# Revit family: HUNTER_PROS-04 Fixed Arc and Adjustable Pro Nozzles
name_source: partatom
category: Sprinklers
revit_build: Autodesk Revit 2017 (Build: 20160225_1515(x64)
units: mm (PartAtom-declared; Revit-internal decimal feet)

## family parameters
Always vertical = Yes
Cut with Voids When Loaded = No
Maintain Annotation Orientation = No
OmniClass Number = 23.11.27.15.11.11
OmniClass Title = Installed Sprinkler Heads
Part Type = Normal
Room Calculation Point = No
Round Connector Dimension = Use Diameter
Shared = Yes
Work Plane-Based = No

## types (24) — shared parameters
Assembly Code = G2050700
Body Height = 155 mm  [stored 0.50853 ft]
Body Material = Hunter® ABS Plastic
Connection_Dia = 15 mm  [stored 0.0492126 ft]
Diameter = 610 mm
Exposed Diameter = 57 mm
Keynote = 328423.02
Manufacturer = Hunter® Industries
Nozzle URL = https://www.hunterindustries.com
Pop Up Height = 100 mm  [stored 0.328084 ft]
Pop Up Material = Hunter® ABS Plastic
Pressure = 210.0 kPa
Seal = Hunter® White Flex Seal
Show 2D Symbol = Yes
Show Water Spray = Yes
Type Comments = Pro-Spray® PROS-04
Type Image = <None>
URL = https://www.hunterindustries.com
Water = Water
Water Spray Pattern = Water Arc

## per-type parameters (varying)
| type | Arc Max | Arc Min | Description | Inlet Size | Model | Nozzle Size | Nozzle_Ref | Trajectory Angle | Trajectory Radius |
| PROS-04-5 Blue-F_360-1.5m | 360.00° | 360.00° | ProSpray® PROS-04 10cm PopUp with Pro-Spray Fixed Arc (5 Blue) Nozzle/ F_360° Arc Position | 1/2'' NPT | PROS-04-5F | Hunter®Pro-Spray Fixed Arc (5 Blue) Nozzle/ F_360° Arc Position | 5000 | 1.00° | 1500 mm  [stored 4.92126 ft] |
| PROS-04-8 Brown-F_360_2.4m | 360.00° | 360.00° | ProSpray® PROS-04 10cm PopUp with Pro-Spray Fixed Arc (8 Brown) Nozzle / F_360° Arc Position | 1/2'' NPT | PROS-04-8F | Hunter®Pro-Spray Fixed Arc (8 Brown) Nozzle / F_360° Arc Position | 8000 | 2.00° | 2400 mm  [stored 7.87402 ft] |
| PROS-04-10 Red-F_360-3.0m | 360.00° | 360.00° | ProSpray® PROS-04 10cm PopUp with Pro-Spray Fixed Arc (10 Red) Nozzle/ F_360° Arc Position | 1/2'' NPT | PROS-04-10F | Hunter®Pro-Spray Fixed Arc (10 Red) Nozzle/ F_360° Arc Position | 10000 | 15.00° | 3000 mm  [stored 9.84252 ft] |
| PROS-04-12 Green-F_360-3.7m | 360.00° | 360.00° | ProSpray® PROS-04 10cm PopUp with Pro-Spray Fixed Arc (12 Green) Nozzle / F_360° Arc Position | 1/2'' NPT | PROS-04-12F | Hunter®Pro-Spray Fixed Arc (12 Green) Nozzle / F_360° Arc Position | 12000 | 28.00° | 3700 mm |
| PROS-04-15 Black-F_360-4.6m | 360.00° | 360.00° | ProSpray® PROS-04 10cm PopUp with Pro-Spray Fixed Arc (15 Black) Nozzle / F_360° Arc Position | 1/2'' NPT | PROS-04-15F | Hunter®Pro-Spray Fixed Arc (15 Black) Nozzle / F_360° Arc Position | 15000 | 28.00° | 4600 mm |
| PROS-04-4A_Lt. Green_1.2m | 360.00° | 0.00° | ProSpray® PROS-04 10cm PopUp with Pro Adjustable 4A-Lt. Green Nozzle | 1/2" NPT | PROS-04-4A | Hunter® Pro Adjustable (4A) Lt.Green Nozzle | 4 | 5.00° | 1200 mm  [stored 3.93701 ft] |
| PROS-04-6A_Lt. Blue_1.8m | 360.00° | 0.00° | ProSpray® PROS-04 10cm PopUp with Pro Adjustable  6A-Lt. Blue Nozzle | 1/2" NPT | PROS-04-6A | Hunter® Pro Adjustable (6A) Lt.Blue Nozzle | 6 | 5.00° | 1800 mm |
| PROS-04-8A_Brown_2.4m | 360.00° | 0.00° | ProSpray® PROS-04 10cm PopUp with Pro Adjustable  8A-Brown Nozzle | 1/2" NPT | PROS-04-8A Brown | Hunter® Pro Adjustable (8A) Brown Nozzle | 8 | 5.00° | 2400 mm  [stored 7.87402 ft] |
| PROS-04-10A_Red_3.0m | 360.00° | 0.00° | ProSpray® PROS-04 10cm PopUp with Pro Adjustable  10A-Red Nozzle | 1/2" NPT | PROS-04-10A Red | Hunter® Pro Adjustable (10A) Red Nozzle | 10 | 15.00° | 3000 mm  [stored 9.84252 ft] |
| PROS-04-12A_Green_3.7m | 360.00° | 0.00° | ProSpray® PROS-04 10cm PopUp with Pro Adjustable  12A-Green Nozzle | 1/2" NPT | PROS-04-12A Green | Hunter® Pro Adjustable (12A) Green Nozzle | 12 | 28.00° | 3700 mm |
| PROS-04-17A_Grey_5.2m | 360.00° | 0.00° | ProSpray® PROS-04 10cm PopUp with Pro Adjustable  17A-Grey Nozzle | 1/2" NPT | PROS-04-17A Grey | Hunter® Pro Adjustable (17A) Grey Nozzle | 17 | 28.00° | 5200 mm |
| PROS-04-15A_Black_4.6m | 360.00° | 0.00° | ProSpray® PROS-04 10cm PopUp with Pro Adjustable  15A-Black Nozzle | 1/2" NPT | PROS-04-15A Black | Hunter® Pro Adjustable (15A) Black Nozzle | 15 | 28.00° | 4600 mm |
| PROS-04-8 Brown-Q_90-2.4m | 90.00° | 90.00° | ProSpray® PROS-04 10cm PopUp with Pro-Spray Fixed Arc (8 Brown) Nozzle / Q_90° Arc Position | 1/2'' NPT | PROS-04-8Q | Hunter®Pro-Spray Fixed Arc (8 Brown) Nozzle / Q_90° Arc Position | 80 | 2.00° | 2400 mm  [stored 7.87402 ft] |
| PROS-04-8 Brown-H_180-2.4m | 180.00° | 180.00° | ProSpray® PROS-04 10cm PopUp with PPro-Spray Fixed Arc (8 Brown) Nozzle / H_180° Arc Position | 1/2'' NPT | PROS-04-8H | Hunter®Pro-Spray Fixed Arc (8 Brown) Nozzle / H_180° Arc Position | 800 | 2.00° | 2400 mm  [stored 7.87402 ft] |
| PROS-04-5 Blue-H_180-1.5m | 180.00° | 180.00° | ProSpray® PROS-04 10cm PopUp with Pro-Spray Fixed Arc (5 Blue) Nozzle/ H_180° Arc Position | 1/2'' NPT | PROS-04-5H | Hunter®Pro-Spray Fixed Arc (5 Blue) Nozzle/ H_180° Arc Position | 500 | 1.00° | 1500 mm  [stored 4.92126 ft] |
| PROS-04-5 Blue-Q_90-1.5m | 90.00° | 90.00° | ProSpray® PROS-04 10cm PopUp with Pro-Spray Fixed Arc (5 Blue) Nozzle / Q_90° Arc Position | 1/2'' NPT | PROS-04-5Q | Hunter®Pro-Spray Fixed Arc (5 Blue) Nozzle / Q_90° Arc Position | 50 | 1.00° | 1500 mm  [stored 4.92126 ft] |
| PROS-04-17 Grey-H_180-5.2m | 180.00° | 180.00° | ProSpray® PROS-04 10cm PopUp with Pro-Spray Fixed Arc (17 Grey) Nozzle / H_180° Arc Position | 1/2'' NPT | PROS-04-17H | Hunter®Pro-Spray Fixed Arc (17 Grey) Nozzle / H_180° Arc Position | 1700 | 28.00° | 5200 mm |
| PROS-04-17 Grey-Q_90-5.2m | 90.00° | 90.00° | ProSpray® PROS-04 10cm PopUp with Pro-Spray Fixed Arc (17 Grey) Nozzle / Q_90° Arc Position | 1/2'' NPT | PROS-04-17Q | Hunter®Pro-Spray Fixed Arc (17 Grey) Nozzle / Q_90° Arc Position | 170 | 28.00° | 5200 mm |
| PROS-04-15 Black-H_180-4.6m | 180.00° | 180.00° | ProSpray® PROS-04 10cm PopUp with Pro-Spray Fixed Arc (15 Black) Nozzle / H_180° Arc Position | 1/2'' NPT | PROS-04-15H | Hunter®Pro-Spray Fixed Arc (15 Black) Nozzle / H_180° Arc Position | 1500 | 28.00° | 4600 mm |
| PROS-04-15 Black-Q_90-4.6m | 90.00° | 90.00° | ProSpray® PROS-04 10cm PopUp with Pro-Spray Fixed Arc (15 Black) Nozzle / Q_90° Arc Position | 1/2'' NPT | PROS-04-15Q | Hunter®Pro-Spray Fixed Arc (15 Black) Nozzle / Q_90° Arc Position | 150 | 28.00° | 4600 mm |
| PROS-04-12 Green-H_180-3.7m | 180.00° | 180.00° | ProSpray® PROS-04 10cm PopUp with Pro-Spray Fixed Arc (12 Green) Nozzle / H_180° Arc Position | 1/2'' NPT | PROS-04-12H | Hunter®Pro-Spray Fixed Arc (12 Green) Nozzle / H_180° Arc Position | 1200 | 28.00° | 3700 mm |
| PROS-04-12 Green-Q_90-3.7m | 90.00° | 90.00° | ProSpray® PROS-04 10cm PopUp with Pro-Spray Fixed Arc (12 Green) Nozzle / Q_90° Arc Position | 1/2'' NPT | PROS-04-12Q | Hunter®Pro-Spray Fixed Arc (12 Green) Nozzle / Q_90° Arc Position | 120 | 28.00° | 3700 mm |
| PROS-04-10 Red-Q_90-3.0m | 90.00° | 90.00° | ProSpray® PROS-04 10cm PopUp with Pro-Spray Fixed Arc (10 Red) Nozzle / Q_90° Arc Position | 1/2'' NPT | PROS-04-10Q | Hunter®Pro-Spray Fixed Arc (10 Red) Nozzle / Q_90° Arc Position | 100 | 15.00° | 3000 mm  [stored 9.84252 ft] |
| PROS-04-10 Red-H_180-3.0m | 180.00° | 180.00° | ProSpray® PROS-04 10cm PopUp with Pro-Spray Fixed Arc (10 Red) Nozzle / H_180° Arc Position | 1/2'' NPT | PROS-04-10H | Hunter®Pro-Spray Fixed Arc (10 Red) Nozzle / H_180° Arc Position | 1000 | 15.00° | 3000 mm  [stored 9.84252 ft] |

note: [stored X ft] marks values corroborated as IEEE doubles in the binary element streams (Revit-internal decimal feet)

## geometry (parser evidence)
native form markers: Sweep x43
no freeform markers — native parametric forms only
